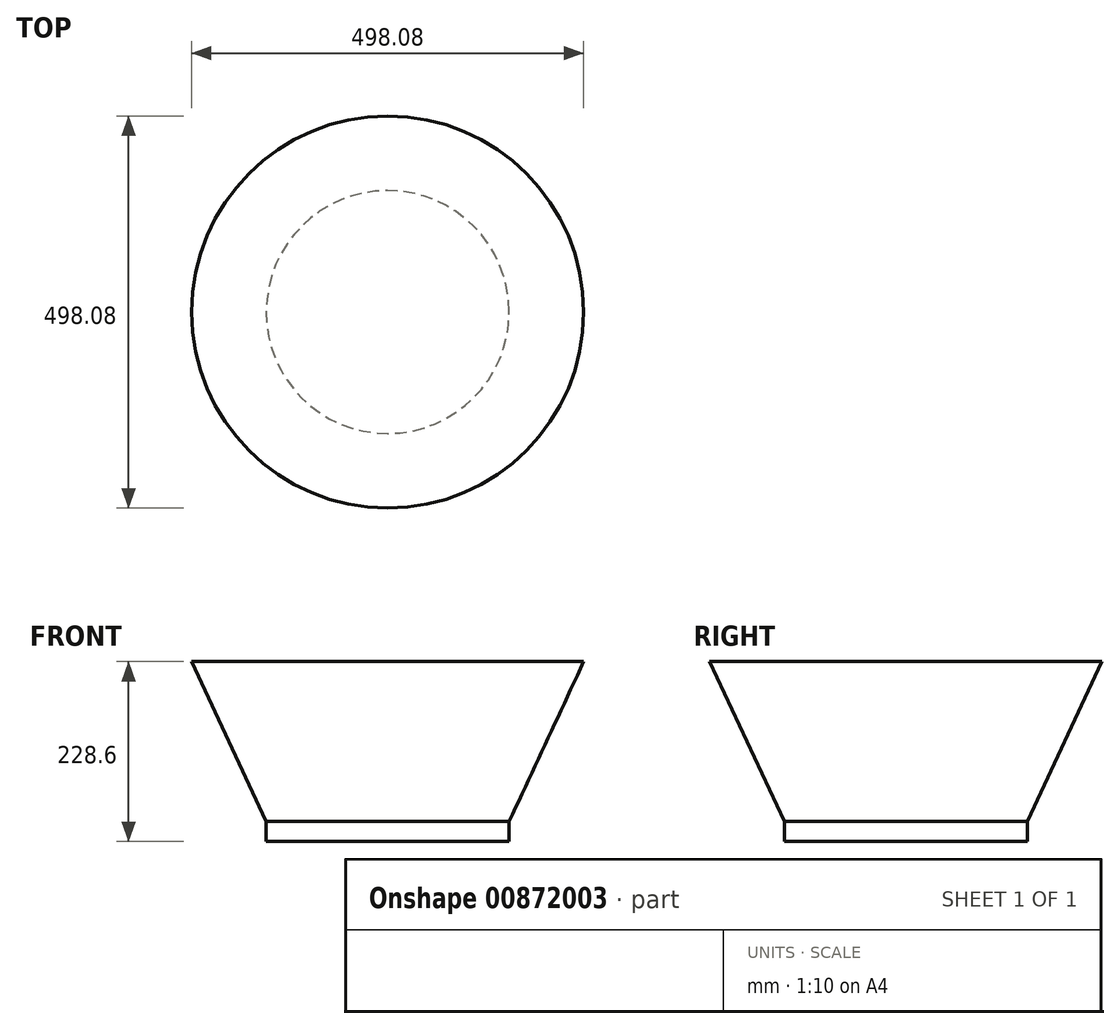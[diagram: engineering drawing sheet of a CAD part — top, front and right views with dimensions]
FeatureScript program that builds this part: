
annotation { "Feature Type Name" : "Feature", "Feature Type Description" : "" }
export const myFeature = defineFeature(function(context is Context, id is Id, definition is map)
    precondition{}
    {
        {
            var Q0;
            Q0=qCreatedBy(makeId("Top.planeOp"),FACE);
            var sketch = newSketch(context, id + "F0", { "sketchPlane" : qUnion([Q0])});
            skCircle(sketch, "E0", {"center": v(0, 0) * mm, "radius": 154.28 * mm});
            skSolve(sketch);
        }
        {
            var Q0;
            Q0=makeQuery(id+"F0.imprint","IMPRINT",FACE,{"disambiguationData":[TD([[makeQuery(id+"F0.imprint","IMPRINT",EDGE,{"derivedFrom":sQuery(id+"F0.wireOp",EDGE,"E0")}),1.0]])]});
            extrude(context, id + "F1", {"entities" : qUnion([Q0]), "depth" : 203.2 * mm, "offsetDistance" : 25.4 * mm, "hasDraft" : true, "draftAngle" : 25 * degree, "hasSecondDirection" : true, "secondDirectionOppositeDirection" : true, "secondDirectionDepth" : 25.4 * mm});
        }
    });
